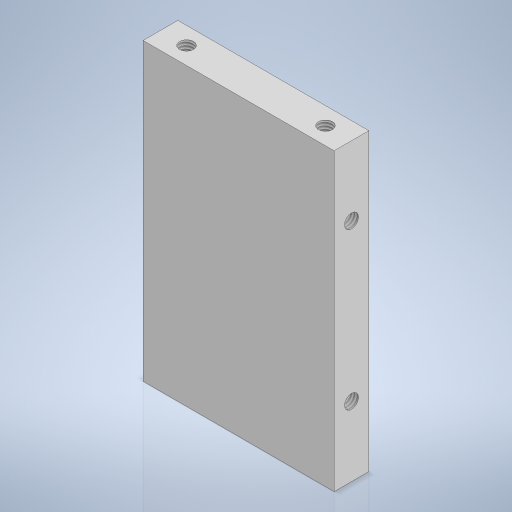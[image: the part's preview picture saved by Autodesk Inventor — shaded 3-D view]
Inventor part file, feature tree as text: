
AUTODESK INVENTOR PART (.ipt)
format: ipt  version: 2024 (Build 280153000, 153)  size: 241,152 bytes
history: native  units: mm
features: sketch x3, hole x2, plane x2, mirror x2, extrude x1
ambient origin geometry x8: Origin, YZ Plane, XZ Plane, XY Plane, X Axis, Y Axis, Z Axis, Center Point
bodies: Volumenkörper1 (feature_tree)
feature tree (10):
  extrude  "Extrusion1"  Depth=68.0mm
  hole  "Bohrung1"  [1 undecoded]
  plane  "Arbeitsebene1"
  mirror  "Spiegeln1"
  hole  "Bohrung2"  [1 undecoded]
  plane  "Arbeitsebene2"
  mirror  "Spiegeln2"
  sketch  "Skizze1"  dims[d0=44.0mm d1=68.0mm]
  sketch  "Skizze2"  dims[d2=8.0mm d3=0.0mm d4=32.0mm]
  sketch  "Skizze3"  dims[d5=6.0mm d6=3.242mm d7=8.0mm d8=4.0mm d9=2.0mm d10=90.0deg d11=10.0mm d12=0.0mm d13=-34.0mm d14=3.242mm d15=8.0mm d16=4.0mm d17=2.0mm d18=90.0deg d19=10.0mm d20=0.0mm d21=16.0mm d22=36.0mm d23=-22.0mm]
note: 2 required parameter values undecoded (feature->parameter linkage not recoverable at this tier; creation-order binding heuristic only, values carry confidence <= 0.55)
